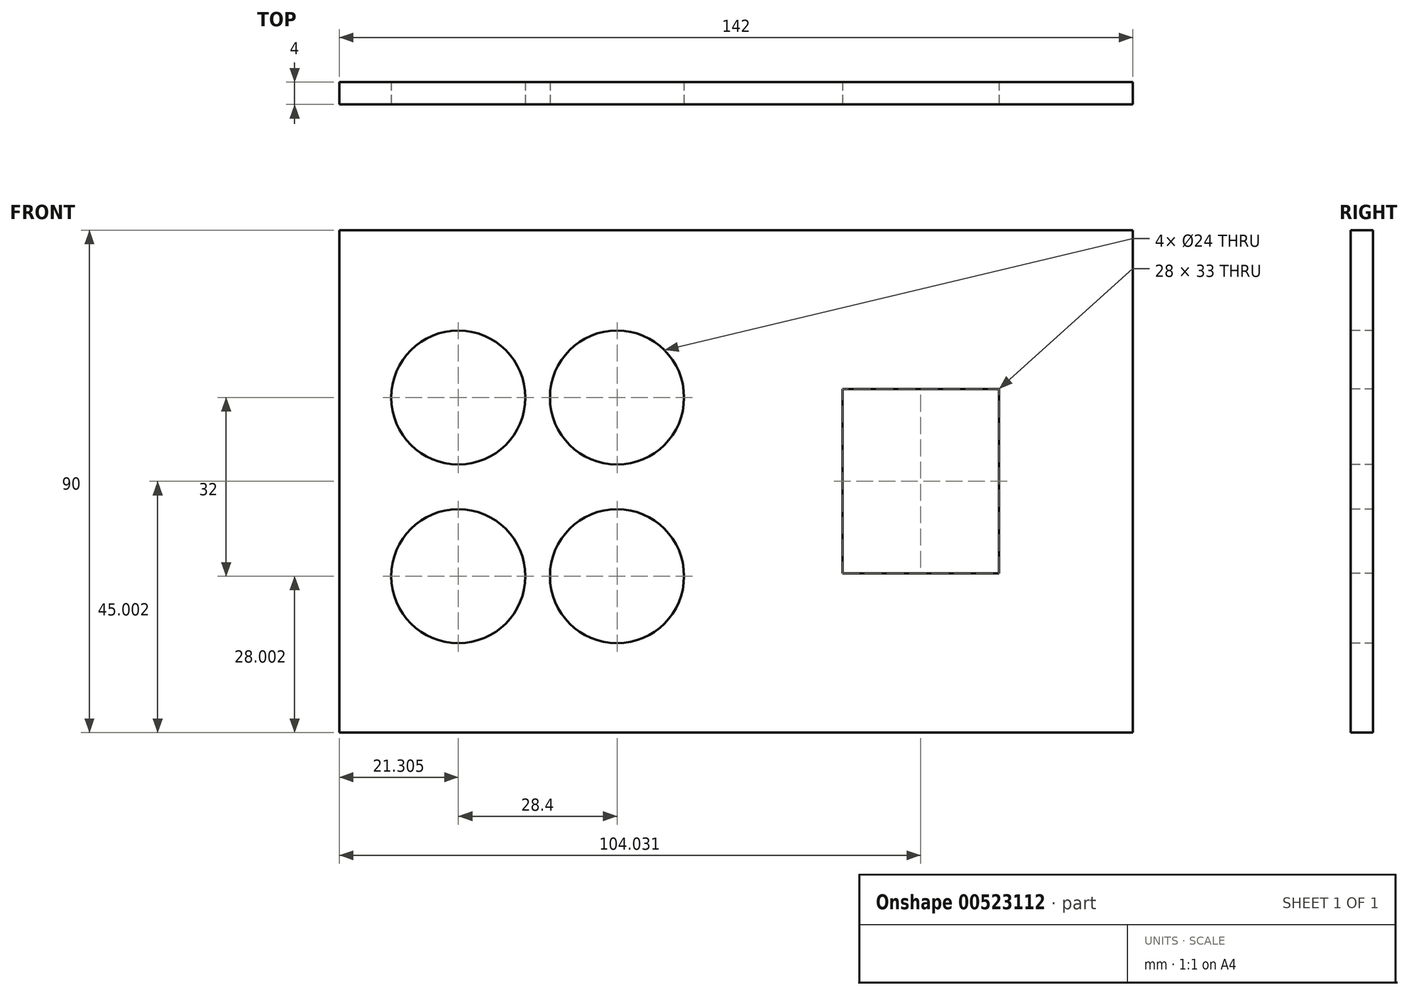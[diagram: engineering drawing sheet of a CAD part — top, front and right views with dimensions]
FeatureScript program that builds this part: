
annotation { "Feature Type Name" : "Feature", "Feature Type Description" : "" }
export const myFeature = defineFeature(function(context is Context, id is Id, definition is map)
    precondition{}
    {
        {
            var Q0;
            Q0=qCreatedBy(makeId("Front.planeOp"),FACE);
            var sketch = newSketch(context, id + "F0", { "sketchPlane" : qUnion([Q0])});
            skLineSegment(sketch, "E0.bottom", {"start": v(-74.88, 46.37) * mm, "end": v(67.12, 46.37) * mm});
            skLineSegment(sketch, "E0.top", {"start": v(-74.88, -43.63) * mm, "end": v(67.12, -43.63) * mm});
            skLineSegment(sketch, "E0.left", {"start": v(-74.88, 46.37) * mm, "end": v(-74.88, -43.63) * mm});
            skLineSegment(sketch, "E0.right", {"start": v(67.12, 46.37) * mm, "end": v(67.12, -43.63) * mm});
            skSolve(sketch);
        }
        {
            var Q0;
            Q0 = qSketchRegion(id + "F0", true);
            extrude(context, id + "F1", {"entities" : qUnion([Q0]), "depth" : 4 * mm, "offsetDistance" : 25 * mm});
        }
        {
            var Q0;
            Q0=makeQuery(id+"F1.opExtrude","CAP_FACE",FACE,{"disambiguationData":[OSD([sQuery(id+"F0.wireOp",EDGE,"E0.bottom"),sQuery(id+"F0.wireOp",EDGE,"E0.top"),sQuery(id+"F0.wireOp",EDGE,"E0.left"),sQuery(id+"F0.wireOp",EDGE,"E0.right")])],"isStart":false});
            var sketch = newSketch(context, id + "F2", { "sketchPlane" : qUnion([Q0])});
            skLineSegment(sketch, "E1", {"start": v(-74.88, 16.37) * mm, "end": v(67.12, 16.37) * mm, "construction": true});
            skCircle(sketch, "E2", {"center": v(-53.58, 16.37) * mm, "radius": 12 * mm});
            skCircle(sketch, "E3", {"center": v(-25.18, 16.37) * mm, "radius": 12 * mm});
            skPoint(sketch, "E4.middle", {"position": v(-59.43, -6.97) * mm});
            skPoint(sketch, "E5.middle", {"position": v(-62.57, -23.63) * mm});
            skLineSegment(sketch, "E6", {"start": v(-74.88, -15.63) * mm, "end": v(67.12, -15.63) * mm, "construction": true});
            skCircle(sketch, "E7", {"center": v(-53.58, -15.63) * mm, "radius": 12 * mm});
            skCircle(sketch, "E8", {"center": v(-25.18, -15.63) * mm, "radius": 12 * mm});
            skLineSegment(sketch, "E9", {"start": v(29.15, -43.63) * mm, "end": v(29.15, 46.37) * mm, "construction": true});
            skLineSegment(sketch, "E10", {"start": v(29.15, 46.37) * mm, "end": v(28, 45.83) * mm, "construction": true});
            skLineSegment(sketch, "E11.bottom", {"start": v(43.15, 17.87) * mm, "end": v(15.15, 17.87) * mm});
            skLineSegment(sketch, "E11.top", {"start": v(43.15, -15.13) * mm, "end": v(15.15, -15.13) * mm});
            skLineSegment(sketch, "E11.left", {"start": v(43.15, 17.87) * mm, "end": v(43.15, -15.13) * mm});
            skLineSegment(sketch, "E11.right", {"start": v(15.15, 17.87) * mm, "end": v(15.15, -15.13) * mm});
            skPoint(sketch, "E11.middle", {"position": v(29.15, 1.37) * mm});
            skSolve(sketch);
        }
        {
            var Q0;
            Q0 = qSketchRegion(id + "F2", true);
            extrude(context, id + "F3", {"entities" : qUnion([Q0]), "operationType" : NewBodyOperationType.REMOVE, "endBound" : BoundingType.THROUGH_ALL, "oppositeDirection" : true, "depth" : 25 * mm, "offsetDistance" : 25 * mm});
        }
    });
